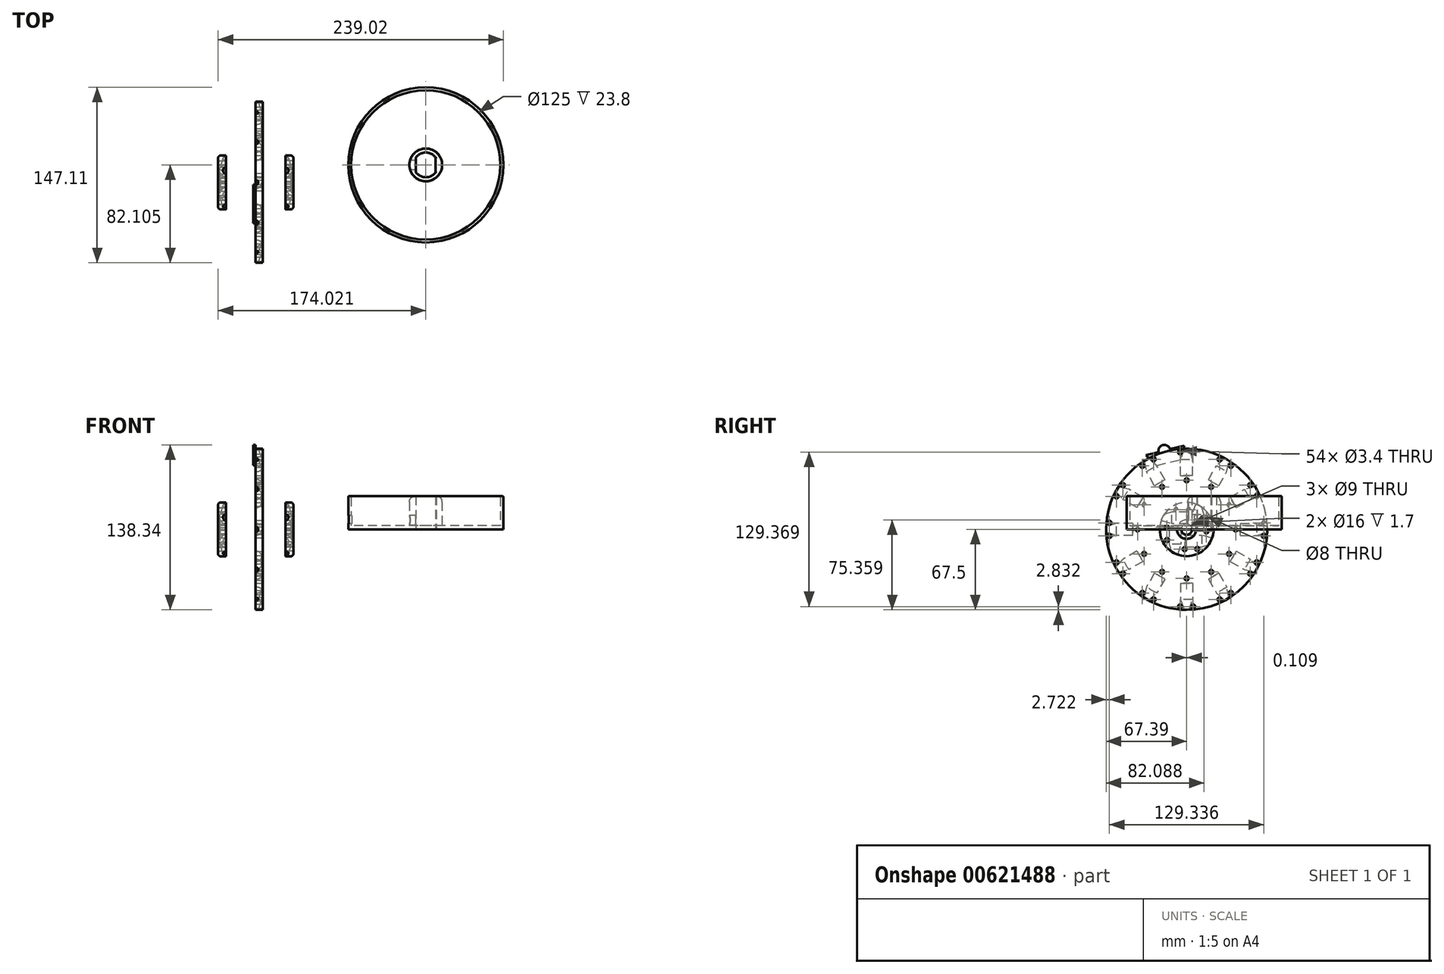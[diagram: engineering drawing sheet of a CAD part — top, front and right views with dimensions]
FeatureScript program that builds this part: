
annotation { "Feature Type Name" : "Feature", "Feature Type Description" : "" }
export const myFeature = defineFeature(function(context is Context, id is Id, definition is map)
    precondition{}
    {
        {
            var Q0;
            Q0=qCreatedBy(makeId("Right.planeOp"),FACE);
            var sketch = newSketch(context, id + "F0", { "sketchPlane" : qUnion([Q0])});
            skCircle(sketch, "E0", {"center": v(0, 0) * mm, "radius": 22.5 * mm});
            skCircle(sketch, "E1", {"center": v(0, 0) * mm, "radius": 4.5 * mm});
            skCircle(sketch, "E2", {"center": v(1.7, 16.57) * mm, "radius": 1.7 * mm});
            skCircle(sketch, "E3", {"center": v(-8.89, 16.41) * mm, "radius": 1.7 * mm});
            skCircle(sketch, "E4.1.0", {"center": v(-16.57, 1.7) * mm, "radius": 1.7 * mm});
            skCircle(sketch, "E4.1.1", {"center": v(-16.41, -8.89) * mm, "radius": 1.7 * mm});
            skCircle(sketch, "E4.2.0", {"center": v(-1.7, -16.57) * mm, "radius": 1.7 * mm});
            skCircle(sketch, "E4.2.1", {"center": v(8.89, -16.41) * mm, "radius": 1.7 * mm});
            skCircle(sketch, "E4.3.0", {"center": v(16.57, -1.7) * mm, "radius": 1.7 * mm});
            skCircle(sketch, "E4.3.1", {"center": v(16.41, 8.89) * mm, "radius": 1.7 * mm});
            skSolve(sketch);
        }
        {
            var Q0;
            Q0=makeQuery(id+"F0.imprint","IMPRINT",FACE,{"disambiguationData":[TD([[makeQuery(id+"F0.imprint","IMPRINT",EDGE,{"derivedFrom":sQuery(id+"F0.wireOp",EDGE,"E0")}),1.0]])]});
            var Q1;
            Q1=makeQuery(id+"F0.imprint","IMPRINT",FACE,{"disambiguationData":[TD([[makeQuery(id+"F0.imprint","IMPRINT",EDGE,{"derivedFrom":sQuery(id+"F0.wireOp",EDGE,"E1")}),-1.0]])]});
            extrude(context, id + "F1", {"entities" : qUnion([Q0, Q1]), "depth" : 6.5 * mm, "offsetDistance" : 25 * mm});
        }
        {
            var Q0;
            Q0=qCreatedBy(makeId("Top.planeOp"),FACE);
            var sketch = newSketch(context, id + "F2", { "sketchPlane" : qUnion([Q0])});
            skLineSegment(sketch, "E5", {"start": v(-19.71, 0) * mm, "end": v(30.41, 0) * mm});
            skSolve(sketch);
        }
        {
            var Q0;
            Q0=qCreatedBy(makeId("Right.planeOp"),FACE);
            var sketch = newSketch(context, id + "F3", { "sketchPlane" : qUnion([Q0])});
            skLineSegment(sketch, "E6.top", {"start": v(1.1, 9.67) * mm, "end": v(1.1, 4.67) * mm});
            skLineSegment(sketch, "E6.left", {"start": v(-12.5, 9.67) * mm, "end": v(1.1, 9.67) * mm});
            skLineSegment(sketch, "E6.right", {"start": v(-12.5, 4.67) * mm, "end": v(1.1, 4.67) * mm});
            skLineSegment(sketch, "E7", {"start": v(-12.5, 4.67) * mm, "end": v(-24.5, 8.57) * mm});
            skLineSegment(sketch, "E8", {"start": v(-24.5, 8.57) * mm, "end": v(-24.5, 9.67) * mm});
            skLineSegment(sketch, "E9", {"start": v(-24.5, 9.67) * mm, "end": v(-12.5, 9.67) * mm});
            skSolve(sketch);
        }
        {
            var Q0;
            Q0=makeQuery(id+"F3.imprint","IMPRINT",FACE,{"disambiguationData":[TD([[makeQuery(id+"F3.imprint","IMPRINT",EDGE,{"derivedFrom":sQuery(id+"F3.wireOp",EDGE,"E6.top")}),-1.0]])]});
            var Q1;
            Q1=sQuery(id+"F3.wireOp",EDGE,"E9");
            revolve(context, id + "F4", {"entities" : qUnion([Q0]), "axis" : qUnion([Q1]), "revolveType" : RevolveType.FULL});
        }
        {
            var Q0;
            Q0=makeQuery(id+"F4.opRevolve","SWEPT_BODY",BODY,{"disambiguationData":[OSD([sQuery(id+"F3.wireOp",EDGE,"E6.top"),sQuery(id+"F3.wireOp",EDGE,"E6.left"),sQuery(id+"F3.wireOp",EDGE,"E6.right"),sQuery(id+"F3.wireOp",EDGE,"E7"),sQuery(id+"F3.wireOp",EDGE,"E8"),sQuery(id+"F3.wireOp",EDGE,"E9")])]});
            var Q1;
            Q1=sQuery(id+"F2.wireOp",EDGE,"E5");
            circularPattern(context, id + "F5", {"entities" : qUnion([Q0]), "axis" : qUnion([Q1]), "angle" : 360 * degree, "instanceCount" : 4, "equalSpace" : true});
        }
        {
            var Q0;
            Q0=makeQuery(id+"F4.opRevolve","SWEPT_BODY",BODY,{"disambiguationData":[OSD([sQuery(id+"F3.wireOp",EDGE,"E6.top"),sQuery(id+"F3.wireOp",EDGE,"E6.left"),sQuery(id+"F3.wireOp",EDGE,"E6.right"),sQuery(id+"F3.wireOp",EDGE,"E7"),sQuery(id+"F3.wireOp",EDGE,"E8"),sQuery(id+"F3.wireOp",EDGE,"E9")])]});
            var Q1;
            Q1=makeQuery(id+"F5.opPattern","COPY",BODY,{"derivedFrom":makeQuery(id+"F4.opRevolve","SWEPT_BODY",BODY,{"disambiguationData":[OSD([sQuery(id+"F3.wireOp",EDGE,"E6.top"),sQuery(id+"F3.wireOp",EDGE,"E6.left"),sQuery(id+"F3.wireOp",EDGE,"E6.right"),sQuery(id+"F3.wireOp",EDGE,"E7"),sQuery(id+"F3.wireOp",EDGE,"E8"),sQuery(id+"F3.wireOp",EDGE,"E9")])]}),"instanceName":"3"});
            var Q2;
            Q2=makeQuery(id+"F5.opPattern","COPY",BODY,{"derivedFrom":makeQuery(id+"F4.opRevolve","SWEPT_BODY",BODY,{"disambiguationData":[OSD([sQuery(id+"F3.wireOp",EDGE,"E6.top"),sQuery(id+"F3.wireOp",EDGE,"E6.left"),sQuery(id+"F3.wireOp",EDGE,"E6.right"),sQuery(id+"F3.wireOp",EDGE,"E7"),sQuery(id+"F3.wireOp",EDGE,"E8"),sQuery(id+"F3.wireOp",EDGE,"E9")])]}),"instanceName":"2"});
            var Q3;
            Q3=makeQuery(id+"F5.opPattern","COPY",BODY,{"derivedFrom":makeQuery(id+"F4.opRevolve","SWEPT_BODY",BODY,{"disambiguationData":[OSD([sQuery(id+"F3.wireOp",EDGE,"E6.top"),sQuery(id+"F3.wireOp",EDGE,"E6.left"),sQuery(id+"F3.wireOp",EDGE,"E6.right"),sQuery(id+"F3.wireOp",EDGE,"E7"),sQuery(id+"F3.wireOp",EDGE,"E8"),sQuery(id+"F3.wireOp",EDGE,"E9")])]}),"instanceName":"1"});
            var Q4;
            Q4=makeQuery(id+"F1.opExtrude","SWEPT_BODY",BODY,{"disambiguationData":[OSD([sQuery(id+"F0.wireOp",EDGE,"E0"),sQuery(id+"F0.wireOp",EDGE,"E1"),sQuery(id+"F0.wireOp",EDGE,"E2"),sQuery(id+"F0.wireOp",EDGE,"cbc2b849-6399-4062-8aac-5185108daa26.1.0"),sQuery(id+"F0.wireOp",EDGE,"cbc2b849-6399-4062-8aac-5185108daa26.2.0"),sQuery(id+"F0.wireOp",EDGE,"cbc2b849-6399-4062-8aac-5185108daa26.3.0")])]});
            booleanBodies(context, id + "F6", {"operationType" : BooleanOperationType.SUBTRACTION, "tools" : qUnion([Q0, Q1, Q2, Q3]), "targets" : qUnion([Q4])});
        }
        {
            var Q0;
            Q0=qCreatedBy(makeId("Right.planeOp"),FACE);
            cPlane(context, id + "F7", {"entities" : qUnion([Q0]), "cplaneType" : CPlaneType.OFFSET, "offset" : 25 * mm, "oppositeDirection" : true, "width" : 150 * mm, "height" : 150 * mm});
        }
        {
            var Q0;
            Q0=makeQuery(id+"F1.opExtrude","CAP_EDGE",EDGE,{"disambiguationData":[OSD([sQuery(id+"F0.wireOp",EDGE,"E0")])],"isStart":false});
            fillet(context, id + "F8", {"entities" : qUnion([Q0]), "radius" : 2 * mm, "tangentPropagation" : true, "allowEdgeOverflow" : false});
        }
        {
            var Q0;
            Q0=makeQuery(id+"F1.opExtrude","CAP_FACE",FACE,{"disambiguationData":[OSD([sQuery(id+"F0.wireOp",EDGE,"E0"),sQuery(id+"F0.wireOp",EDGE,"E1"),sQuery(id+"F0.wireOp",EDGE,"E2"),sQuery(id+"F0.wireOp",EDGE,"E3"),sQuery(id+"F0.wireOp",EDGE,"E4.1.0"),sQuery(id+"F0.wireOp",EDGE,"E4.1.1"),sQuery(id+"F0.wireOp",EDGE,"E4.2.0"),sQuery(id+"F0.wireOp",EDGE,"E4.2.1"),sQuery(id+"F0.wireOp",EDGE,"E4.3.0"),sQuery(id+"F0.wireOp",EDGE,"E4.3.1")])],"isStart":false});
            var sketch = newSketch(context, id + "F9", { "sketchPlane" : qUnion([Q0])});
            skCircle(sketch, "E10", {"center": v(0, 0) * mm, "radius": 8 * mm});
            skSolve(sketch);
        }
        {
            var Q0;
            Q0=makeQuery(id+"F9.imprint","IMPRINT",FACE,{"disambiguationData":[TD([[makeQuery(id+"F9.imprint","IMPRINT",EDGE,{"derivedFrom":sQuery(id+"F9.wireOp",EDGE,"E10")}),1.0]])]});
            extrude(context, id + "F10", {"entities" : qUnion([Q0]), "operationType" : NewBodyOperationType.REMOVE, "oppositeDirection" : true, "depth" : 1.7 * mm, "offsetDistance" : 25 * mm});
        }
        {
            var Q0;
            Q0=makeQuery(id+"F1.opExtrude","SWEPT_BODY",BODY,{"disambiguationData":[OSD([sQuery(id+"F0.wireOp",EDGE,"E0"),sQuery(id+"F0.wireOp",EDGE,"E1"),sQuery(id+"F0.wireOp",EDGE,"E2"),sQuery(id+"F0.wireOp",EDGE,"cbc2b849-6399-4062-8aac-5185108daa26.1.0"),sQuery(id+"F0.wireOp",EDGE,"cbc2b849-6399-4062-8aac-5185108daa26.2.0"),sQuery(id+"F0.wireOp",EDGE,"cbc2b849-6399-4062-8aac-5185108daa26.3.0")])]});
            var Q1;
            Q1=qCreatedBy(id+"F7.planeOp",FACE);
            mirror(context, id + "F11", {"entities" : qUnion([Q0]), "mirrorPlane" : qUnion([Q1])});
        }
        {
            var Q0;
            Q0=qCreatedBy(makeId("Top.planeOp"),FACE);
            var sketch = newSketch(context, id + "F12", { "sketchPlane" : qUnion([Q0])});
            skArc(sketch, "E11", {"start": v(125.77, 20.98) * mm, "mid": v(117.52, 25.08) * mm, "end": v(109.27, 20.98) * mm});
            skArc(sketch, "E12.trimOffspring", {"start": v(109.27, 8.45) * mm, "mid": v(117.52, 4.35) * mm, "end": v(125.77, 8.45) * mm});
            skLineSegment(sketch, "E13.trimOffspring", {"start": v(109.27, 8.45) * mm, "end": v(109.27, 20.98) * mm});
            skLineSegment(sketch, "E14", {"start": v(126.84, 20.76) * mm, "end": v(126.62, 20.47) * mm});
            skLineSegment(sketch, "E15", {"start": v(126.62, 20.47) * mm, "end": v(126.84, 20.3) * mm});
            skLineSegment(sketch, "E16", {"start": v(126.84, 8.77) * mm, "end": v(126.62, 8.56) * mm});
            skLineSegment(sketch, "E17", {"start": v(126.62, 8.56) * mm, "end": v(126.84, 8.33) * mm});
            skLineSegment(sketch, "E18", {"start": v(125.77, 8.45) * mm, "end": v(126.16, 8.56) * mm});
            skLineSegment(sketch, "E19", {"start": v(126.16, 8.56) * mm, "end": v(125.77, 8.97) * mm});
            skLineSegment(sketch, "E20", {"start": v(125.77, 8.97) * mm, "end": v(125.77, 20.43) * mm});
            skLineSegment(sketch, "E21", {"start": v(125.77, 20.43) * mm, "end": v(126.2, 20.72) * mm});
            skLineSegment(sketch, "E22", {"start": v(126.2, 20.72) * mm, "end": v(125.77, 20.98) * mm});
            skCircle(sketch, "E23", {"center": v(117.52, 14.72) * mm, "radius": 65 * mm});
            skCircle(sketch, "E24", {"center": v(117.52, 14.72) * mm, "radius": 13.7 * mm});
            skCircle(sketch, "E25", {"center": v(117.52, 14.72) * mm, "radius": 62.5 * mm});
            skSolve(sketch);
        }
        {
            var Q0;
            Q0=makeQuery(id+"F12.imprint","IMPRINT",FACE,{"disambiguationData":[TD([[makeQuery(id+"F12.imprint","IMPRINT",EDGE,{"derivedFrom":sQuery(id+"F12.wireOp",EDGE,"E23")}),1.0]])]});
            var Q1;
            Q1=makeQuery(id+"F12.imprint","IMPRINT",FACE,{"disambiguationData":[TD([[makeQuery(id+"F12.imprint","IMPRINT",EDGE,{"derivedFrom":sQuery(id+"F12.wireOp",EDGE,"E11")}),-1.0]])]});
            var Q2;
            Q2=makeQuery(id+"F12.imprint","IMPRINT",FACE,{"disambiguationData":[TD([[makeQuery(id+"F12.imprint","IMPRINT",EDGE,{"derivedFrom":sQuery(id+"F12.wireOp",EDGE,"E24")}),-1.0]])]});
            extrude(context, id + "F13", {"entities" : qUnion([Q0, Q1, Q2]), "depth" : 3 * mm, "offsetDistance" : 25 * mm});
        }
        {
            var Q0;
            Q0=makeQuery(id+"F12.imprint","IMPRINT",FACE,{"disambiguationData":[TD([[makeQuery(id+"F12.imprint","IMPRINT",EDGE,{"derivedFrom":sQuery(id+"F12.wireOp",EDGE,"E11")}),-1.0]])]});
            var Q1;
            Q1=makeQuery(id+"F12.imprint","IMPRINT",FACE,{"disambiguationData":[TD([[makeQuery(id+"F12.imprint","IMPRINT",EDGE,{"derivedFrom":sQuery(id+"F12.wireOp",EDGE,"E23")}),1.0]])]});
            extrude(context, id + "F14", {"entities" : qUnion([Q0, Q1]), "operationType" : NewBodyOperationType.ADD, "depth" : 28 * mm, "offsetDistance" : 25 * mm});
        }
        {
            var Q0;
            Q0=makeQuery(id+"F13.opExtrude","CAP_EDGE",EDGE,{"disambiguationData":[OSD([sQuery(id+"F12.wireOp",EDGE,"E23")])],"isStart":false});
            var Q1;
            Q1=makeQuery(id+"F14.opExtrude","CAP_EDGE",EDGE,{"disambiguationData":[OSD([sQuery(id+"F12.wireOp",EDGE,"E24")])],"isStart":false});
            fillet(context, id + "F15", {"entities" : qUnion([Q0, Q1]), "radius" : 5 * mm, "tangentPropagation" : true, "allowEdgeOverflow" : false});
        }
        {
            var Q0;
            {var subQ0=sQuery(id+"F12.wireOp",EDGE,"E13.trimOffspring");Q0=makeQuery(id+"F14.boolean.opBoolean","MERGE",FACE,{"derivedFrom":[makeQuery(id+"F13.opExtrude","SWEPT_FACE",FACE,{"disambiguationData":[OSD([subQ0])]}),makeQuery(id+"F14.opExtrude","SWEPT_FACE",FACE,{"disambiguationData":[OSD([subQ0])]})]});}
            var sketch = newSketch(context, id + "F16", { "sketchPlane" : qUnion([Q0])});
            skCircle(sketch, "E26", {"center": v(14.7, 7.86) * mm, "radius": 4 * mm});
            skPoint(sketch, "E26.centerSnap0", {"position": v(20.98, 13.86) * mm});
            skSolve(sketch);
        }
        {
            var Q0;
            Q0=makeQuery(id+"F16.imprint","IMPRINT",FACE,{"disambiguationData":[TD([[makeQuery(id+"F16.imprint","IMPRINT",EDGE,{"derivedFrom":sQuery(id+"F16.wireOp",EDGE,"E26")}),1.0]])]});
            extrude(context, id + "F17", {"entities" : qUnion([Q0]), "operationType" : NewBodyOperationType.REMOVE, "oppositeDirection" : true, "depth" : 25 * mm, "offsetDistance" : 25 * mm});
        }
        {
            var Q0;
            {var subQ0=sQuery(id+"F12.wireOp",EDGE,"E13.trimOffspring");Q0=makeQuery(id+"F14.boolean.opBoolean","MERGE",FACE,{"derivedFrom":[makeQuery(id+"F13.opExtrude","SWEPT_FACE",FACE,{"disambiguationData":[OSD([subQ0])]}),makeQuery(id+"F14.opExtrude","SWEPT_FACE",FACE,{"disambiguationData":[OSD([subQ0])]})]});}
            cPlane(context, id + "F18", {"entities" : qUnion([Q0]), "cplaneType" : CPlaneType.OFFSET, "offset" : 60 * mm, "oppositeDirection" : true, "width" : 150 * mm, "height" : 150 * mm});
        }
        {
            var Q0;
            Q0=qCreatedBy(id+"F18.planeOp",FACE);
            var sketch = newSketch(context, id + "F19", { "sketchPlane" : qUnion([Q0])});
            skPoint(sketch, "E27.firstSnap0", {"position": v(22, 8) * mm});
            skLineSegment(sketch, "E27.bottom", {"start": v(6.3, 4.8) * mm, "end": v(21.3, 4.8) * mm});
            skLineSegment(sketch, "E27.top", {"start": v(6.3, 11.8) * mm, "end": v(21.3, 11.8) * mm});
            skLineSegment(sketch, "E27.left", {"start": v(6.3, 4.8) * mm, "end": v(6.3, 11.8) * mm});
            skLineSegment(sketch, "E27.right", {"start": v(21.3, 4.8) * mm, "end": v(21.3, 11.8) * mm});
            skSolve(sketch);
        }
        {
            var Q0;
            Q0=makeQuery(id+"F19.imprint","IMPRINT",FACE,{"disambiguationData":[TD([[makeQuery(id+"F19.imprint","IMPRINT",EDGE,{"derivedFrom":sQuery(id+"F19.wireOp",EDGE,"E27.bottom")}),1.0]])]});
            extrude(context, id + "F20", {"entities" : qUnion([Q0]), "operationType" : NewBodyOperationType.REMOVE, "depth" : 10 * mm, "offsetDistance" : 25 * mm});
        }
        {
            var Q0;
            Q0=makeQuery(id+"F14.opExtrude","CAP_EDGE",EDGE,{"disambiguationData":[OSD([sQuery(id+"F12.wireOp",EDGE,"E23")])],"isStart":false});
            var Q1;
            Q1=makeQuery(id+"F14.opExtrude","CAP_EDGE",EDGE,{"disambiguationData":[OSD([sQuery(id+"F12.wireOp",EDGE,"E25")])],"isStart":false});
            fillet(context, id + "F21", {"entities" : qUnion([Q0, Q1]), "radius" : 1.2 * mm, "tangentPropagation" : true, "allowEdgeOverflow" : false});
        }
        {
            var Q0;
            Q0=qCreatedBy(id+"F7.planeOp",FACE);
            var sketch = newSketch(context, id + "F22", { "sketchPlane" : qUnion([Q0])});
            skCircle(sketch, "E28", {"center": v(0.1, 0) * mm, "radius": 67.5 * mm});
            skLineSegment(sketch, "E29.top", {"start": v(-45.16, 0) * mm, "end": v(-45.16, -5) * mm});
            skLineSegment(sketch, "E29.left", {"start": v(-58.76, 0) * mm, "end": v(-45.16, 0) * mm});
            skLineSegment(sketch, "E29.right", {"start": v(-58.76, -5) * mm, "end": v(-45.16, -5) * mm});
            skLineSegment(sketch, "E30", {"start": v(-58.76, -5) * mm, "end": v(-70.76, -1.1) * mm});
            skLineSegment(sketch, "E31", {"start": v(-70.76, -1.1) * mm, "end": v(-70.76, 0) * mm});
            skLineSegment(sketch, "E32", {"start": v(-70.76, 0) * mm, "end": v(-58.76, 0) * mm});
            skLineSegment(sketch, "E33", {"start": v(0.1, 0) * mm, "end": v(73.26, 0) * mm, "construction": true});
            skLineSegment(sketch, "E34", {"start": v(-1.5, 0) * mm, "end": v(-77.5, 0) * mm, "construction": true});
            skCircle(sketch, "E35", {"center": v(0.1, 0) * mm, "radius": 4.5 * mm});
            skCircle(sketch, "E36", {"center": v(-64.67, -5.5) * mm, "radius": 1.7 * mm});
            skLineSegment(sketch, "E37", {"start": v(-64.67, -5.5) * mm, "end": v(-64.67, 5.19) * mm, "construction": true});
            skCircle(sketch, "E38", {"center": v(-64.67, 5.5) * mm, "radius": 1.7 * mm});
            skCircle(sketch, "E39.1.0", {"center": v(-53.25, -37.1) * mm, "radius": 1.7 * mm});
            skCircle(sketch, "E39.1.1", {"center": v(-58.75, -27.57) * mm, "radius": 1.7 * mm});
            skCircle(sketch, "E39.2.0", {"center": v(-27.57, -58.75) * mm, "radius": 1.7 * mm});
            skCircle(sketch, "E39.2.1", {"center": v(-37.1, -53.25) * mm, "radius": 1.7 * mm});
            skCircle(sketch, "E39.3.0", {"center": v(5.5, -64.67) * mm, "radius": 1.7 * mm});
            skCircle(sketch, "E39.3.1", {"center": v(-5.5, -64.67) * mm, "radius": 1.7 * mm});
            skCircle(sketch, "E39.4.0", {"center": v(37.1, -53.25) * mm, "radius": 1.7 * mm});
            skCircle(sketch, "E39.4.1", {"center": v(27.57, -58.75) * mm, "radius": 1.7 * mm});
            skCircle(sketch, "E39.5.0", {"center": v(58.75, -27.57) * mm, "radius": 1.7 * mm});
            skCircle(sketch, "E39.5.1", {"center": v(53.25, -37.1) * mm, "radius": 1.7 * mm});
            skCircle(sketch, "E39.6.0", {"center": v(64.67, 5.5) * mm, "radius": 1.7 * mm});
            skCircle(sketch, "E39.6.1", {"center": v(64.67, -5.5) * mm, "radius": 1.7 * mm});
            skCircle(sketch, "E39.7.0", {"center": v(53.25, 37.1) * mm, "radius": 1.7 * mm});
            skCircle(sketch, "E39.7.1", {"center": v(58.75, 27.57) * mm, "radius": 1.7 * mm});
            skCircle(sketch, "E39.8.0", {"center": v(27.57, 58.75) * mm, "radius": 1.7 * mm});
            skCircle(sketch, "E39.8.1", {"center": v(37.1, 53.25) * mm, "radius": 1.7 * mm});
            skCircle(sketch, "E39.9.0", {"center": v(-5.5, 64.67) * mm, "radius": 1.7 * mm});
            skCircle(sketch, "E39.9.1", {"center": v(5.5, 64.67) * mm, "radius": 1.7 * mm});
            skCircle(sketch, "E39.10.0", {"center": v(-37.1, 53.25) * mm, "radius": 1.7 * mm});
            skCircle(sketch, "E39.10.1", {"center": v(-27.57, 58.75) * mm, "radius": 1.7 * mm});
            skCircle(sketch, "E39.11.0", {"center": v(-58.75, 27.57) * mm, "radius": 1.7 * mm});
            skCircle(sketch, "E39.11.1", {"center": v(-53.25, 37.1) * mm, "radius": 1.7 * mm});
            skPoint(sketch, "E39.center", {"position": v(0, 0) * mm});
            skCircle(sketch, "E40", {"center": v(-41.1, 0) * mm, "radius": 1.7 * mm});
            skCircle(sketch, "E41.1.0", {"center": v(-35.6, -20.55) * mm, "radius": 1.7 * mm});
            skCircle(sketch, "E41.2.0", {"center": v(-20.55, -35.6) * mm, "radius": 1.7 * mm});
            skCircle(sketch, "E41.3.0", {"center": v(0, -41.1) * mm, "radius": 1.7 * mm});
            skCircle(sketch, "E41.4.0", {"center": v(20.55, -35.6) * mm, "radius": 1.7 * mm});
            skCircle(sketch, "E41.5.0", {"center": v(35.6, -20.55) * mm, "radius": 1.7 * mm});
            skCircle(sketch, "E41.6.0", {"center": v(41.1, 0) * mm, "radius": 1.7 * mm});
            skCircle(sketch, "E41.7.0", {"center": v(35.6, 20.55) * mm, "radius": 1.7 * mm});
            skCircle(sketch, "E41.8.0", {"center": v(20.55, 35.6) * mm, "radius": 1.7 * mm});
            skCircle(sketch, "E41.9.0", {"center": v(0, 41.1) * mm, "radius": 1.7 * mm});
            skCircle(sketch, "E41.10.0", {"center": v(-20.55, 35.6) * mm, "radius": 1.7 * mm});
            skCircle(sketch, "E41.11.0", {"center": v(-35.6, 20.55) * mm, "radius": 1.7 * mm});
            skSolve(sketch);
        }
        {
            var Q0;
            Q0=makeQuery(id+"F22.imprint","IMPRINT",FACE,{"disambiguationData":[TD([[makeQuery(id+"F22.imprint","IMPRINT",EDGE,{"derivedFrom":sQuery(id+"F22.wireOp",EDGE,"E29.top")}),1.0]])]});
            var Q1;
            Q1=makeQuery(id+"F22.imprint","IMPRINT",FACE,{"disambiguationData":[TD([[makeQuery(id+"F22.imprint","IMPRINT",EDGE,{"derivedFrom":sQuery(id+"F22.wireOp",EDGE,"E29.top")}),-1.0]])]});
            var Q2;
            Q2=sQuery(id+"F22.wireOp",EDGE,"E28");
            extrude(context, id + "F23", {"entities" : qUnion([Q0, Q1]), "surfaceEntities" : qUnion([Q2]), "depth" : 6 * mm, "offsetDistance" : 25 * mm});
        }
        {
            var Q0;
            Q0=makeQuery(id+"F22.imprint","IMPRINT",FACE,{"disambiguationData":[TD([[makeQuery(id+"F22.imprint","IMPRINT",EDGE,{"derivedFrom":sQuery(id+"F22.wireOp",EDGE,"E29.top")}),-1.0]])]});
            var Q1;
            {var subQ5=sQuery(id+"F22.wireOp",EDGE,"E31");Q1=makeQuery(id+"F22.imprint","IMPRINT",FACE,{"disambiguationData":[TD([[makeQuery(id+"F22.imprint","IMPRINT",EDGE,{"derivedFrom":subQ5}),-1.0]])]});}
            var Q2;
            Q2=sQuery(id+"F22.wireOp",EDGE,"E29.left");
            revolve(context, id + "F24", {"surfaceOperationType" : NewSurfaceOperationType.NEW, "entities" : qUnion([Q0, Q1]), "axis" : qUnion([Q2]), "revolveType" : RevolveType.FULL});
        }
        {
            var Q0;
            Q0=sQuery(id+"F22.wireOp",VERTEX,"E33.start");
            var Q1;
            Q1=sQuery(id+"F12.wireOp",VERTEX,"E11.center");
            var Q2;
            Q2=sQuery(id+"F22.wireOp",VERTEX,"E33.end");
            cPlane(context, id + "F25", {"entities" : qUnion([Q0, Q1, Q2]), "cplaneType" : CPlaneType.THREE_POINT, "offset" : 25 * mm, "width" : 150 * mm, "height" : 150 * mm});
        }
        {
            var Q0;
            Q0=makeQuery(id+"F24.opRevolve","SWEPT_BODY",BODY,{"disambiguationData":[OSD([sQuery(id+"F22.wireOp",EDGE,"E28"),sQuery(id+"F22.wireOp",EDGE,"E29.top"),sQuery(id+"F22.wireOp",EDGE,"E29.left"),sQuery(id+"F22.wireOp",EDGE,"E29.right"),sQuery(id+"F22.wireOp",EDGE,"E30"),sQuery(id+"F22.wireOp",EDGE,"E32")])]});
            var Q1;
            Q1=sQuery(id+"F2.wireOp",EDGE,"E5");
            circularPattern(context, id + "F26", {"operationType" : NewBodyOperationType.REMOVE, "entities" : qUnion([Q0]), "axis" : qUnion([Q1]), "angle" : 360 * degree, "instanceCount" : 12, "equalSpace" : true});
        }
        {
            var Q0;
            Q0=makeQuery(id+"F22.imprint","IMPRINT",FACE,{"disambiguationData":[TD([[makeQuery(id+"F22.imprint","IMPRINT",EDGE,{"derivedFrom":sQuery(id+"F22.wireOp",EDGE,"E29.top")}),1.0]])]});
            var sketch = newSketch(context, id + "F27", { "sketchPlane" : qUnion([Q0])});
            skLineSegment(sketch, "E42", {"start": v(-5.56, 58.3) * mm, "end": v(-1.8, 70.19) * mm});
            skLineSegment(sketch, "E43", {"start": v(-1.8, 70.19) * mm, "end": v(-34.14, 62.05) * mm});
            skLineSegment(sketch, "E44", {"start": v(-34.14, 62.05) * mm, "end": v(-24.9, 53.7) * mm});
            skLineSegment(sketch, "E45", {"start": v(-24.9, 53.7) * mm, "end": v(-5.56, 58.3) * mm});
            skCircle(sketch, "E46", {"center": v(-5.45, 64.7) * mm, "radius": 1.7 * mm});
            skCircle(sketch, "E47", {"center": v(-27.57, 58.76) * mm, "radius": 1.7 * mm});
            skArc(sketch, "E48", {"start": v(-13.93, 67.13) * mm, "mid": v(-19.9, 70.69) * mm, "end": v(-23.48, 64.73) * mm});
            skSolve(sketch);
        }
        {
            var Q0;
            Q0 = qSketchRegion(id + "F27", true);
            extrude(context, id + "F28", {"entities" : qUnion([Q0]), "oppositeDirection" : true, "depth" : 2.1 * mm, "offsetDistance" : 25 * mm});
        }
    });
